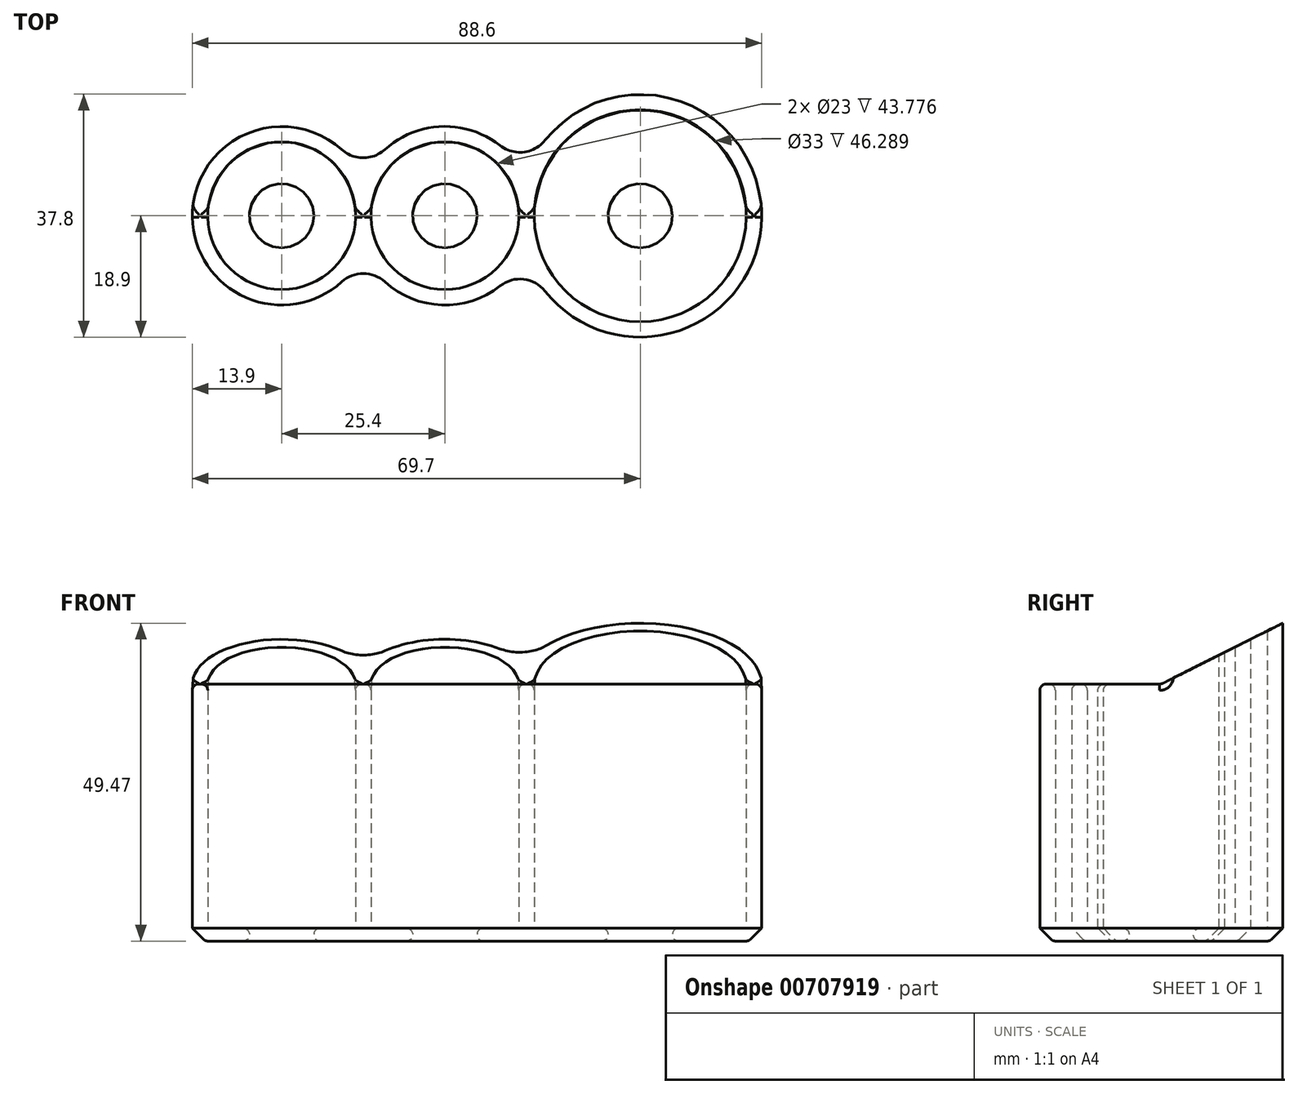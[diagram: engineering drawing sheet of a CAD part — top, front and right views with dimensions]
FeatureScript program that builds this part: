
annotation { "Feature Type Name" : "Feature", "Feature Type Description" : "" }
export const myFeature = defineFeature(function(context is Context, id is Id, definition is map)
    precondition{}
    {
        {
            var Q0;
            Q0=qCreatedBy(makeId("Top.planeOp"),FACE);
            var sketch = newSketch(context, id + "F0", { "sketchPlane" : qUnion([Q0])});
            skCircle(sketch, "E0", {"center": v(30.4, 0) * mm, "radius": 16.5 * mm});
            skCircle(sketch, "E1", {"center": v(0, 0) * mm, "radius": 11.5 * mm});
            skCircle(sketch, "E2", {"center": v(-25.4, 0) * mm, "radius": 11.5 * mm});
            skArc(sketch, "E3.0", {"start": v(-12.7, 5.65) * mm, "mid": v(-39.3, 0) * mm, "end": v(-12.7, -5.65) * mm});
            skArc(sketch, "E4.0", {"start": v(-12.7, -5.65) * mm, "mid": v(-0.23, -13.9) * mm, "end": v(12.5, -6.07) * mm});
            skArc(sketch, "E5.0", {"start": v(12.5, -6.07) * mm, "mid": v(49.3, 0) * mm, "end": v(12.5, 6.07) * mm});
            skArc(sketch, "E6.trimOffspring", {"start": v(12.5, 6.07) * mm, "mid": v(-0.23, 13.9) * mm, "end": v(-12.7, 5.65) * mm});
            skSolve(sketch);
        }
        {
            var Q0;
            Q0=qSketchRegion(id+"F0",true);
            extrude(context, id + "F1", {"entities" : qUnion([Q0]), "depth" : 50 * mm, "offsetDistance" : 25 * mm});
        }
        {
            var Q0;
            Q0=makeQuery(id+"F1.opExtrude","SWEPT_EDGE",EDGE,{"disambiguationData":[OSD([sQuery(id+"F0.wireOp",EDGE,"E3.0"),sQuery(id+"F0.wireOp",EDGE,"E4.0")])]});
            var Q1;
            Q1=makeQuery(id+"F1.opExtrude","SWEPT_EDGE",EDGE,{"disambiguationData":[OSD([sQuery(id+"F0.wireOp",EDGE,"E3.0"),sQuery(id+"F0.wireOp",EDGE,"E6.trimOffspring")])]});
            var Q2;
            Q2=makeQuery(id+"F1.opExtrude","SWEPT_EDGE",EDGE,{"disambiguationData":[OSD([sQuery(id+"F0.wireOp",EDGE,"E5.0"),sQuery(id+"F0.wireOp",EDGE,"E6.trimOffspring")])]});
            var Q3;
            Q3=makeQuery(id+"F1.opExtrude","SWEPT_EDGE",EDGE,{"disambiguationData":[OSD([sQuery(id+"F0.wireOp",EDGE,"E4.0"),sQuery(id+"F0.wireOp",EDGE,"E5.0")])]});
            fillet(context, id + "F2", {"entities" : qUnion([Q0, Q1, Q2, Q3]), "tangentPropagation" : true, "radius" : 5 * mm, "defaultsChanged" : false, "vertexSettings" : [], "allowEdgeOverflow" : false});
        }
        {
            var Q0;
            Q0=makeQuery(id+"F1.opExtrude","CAP_FACE",FACE,{"disambiguationData":[OSD([sQuery(id+"F0.wireOp",EDGE,"E0"),sQuery(id+"F0.wireOp",EDGE,"bsvTM2Ju-xRZ2-JFpn-cVXU-KiCRrkx4IUK1"),sQuery(id+"F0.wireOp",EDGE,"E1"),sQuery(id+"F0.wireOp",EDGE,"H1CsF2ZF-1dV5-S10X-kmG2-70JKXfVExCmK"),sQuery(id+"F0.wireOp",EDGE,"zndfJJh6-VviL-ZSxk-hczQ-EYFnHKfXtcnA"),sQuery(id+"F0.wireOp",EDGE,"HC5cK6VC-82Qt-4upF-mIoj-Tu8vghqNYBpw"),sQuery(id+"F0.wireOp",EDGE,"rIxCz0YV-udHC-Ne6c-NjN8-CFdPHwDd2JFN"),sQuery(id+"F0.wireOp",EDGE,"U2L2fL6y-dszB-5rkY-noFO-yn2avRcztpQ9"),sQuery(id+"F0.wireOp",EDGE,"qxlrs1d4-wGFa-lEeD-9ZLo-S0vqTRGAxUW6")])],"isStart":true});
            var sketch = newSketch(context, id + "F3", { "sketchPlane" : qUnion([Q0])});
            skCircle(sketch, "E7.0", {"center": v(-25.4, 0) * mm, "radius": 11.5 * mm});
            skCircle(sketch, "E8.0", {"center": v(0, 0) * mm, "radius": 11.5 * mm});
            skCircle(sketch, "E9", {"center": v(-25.4, 0) * mm, "radius": 5 * mm});
            skCircle(sketch, "E10", {"center": v(0, 0) * mm, "radius": 5 * mm});
            skCircle(sketch, "E11.0", {"center": v(30.4, 0) * mm, "radius": 16.5 * mm});
            skCircle(sketch, "E12", {"center": v(30.4, 0) * mm, "radius": 5 * mm});
            skSolve(sketch);
        }
        {
            var Q0;
            Q0 = qSketchRegion(id + "F3", true);
            extrude(context, id + "F4", {"entities" : qUnion([Q0]), "operationType" : NewBodyOperationType.ADD, "oppositeDirection" : true, "depth" : 2 * mm, "offsetDistance" : 25 * mm});
        }
        {
            var Q0;
            Q0=makeQuery(id+"F1.opExtrude","CAP_EDGE",EDGE,{"disambiguationData":[OSD([sQuery(id+"F0.wireOp",EDGE,"E5.0")])],"isStart":true});
            chamfer(context, id + "F5", {"entities" : qUnion([Q0]), "width" : 2 * mm, "tangentPropagation" : true});
        }
        {
            var Q0;
            Q0=qCreatedBy(makeId("Right.planeOp"),FACE);
            var sketch = newSketch(context, id + "F6", { "sketchPlane" : qUnion([Q0])});
            skLineSegment(sketch, "E13", {"start": v(19.97, 50) * mm, "end": v(0, 40) * mm});
            skLineSegment(sketch, "E14", {"start": v(-28.18, 50) * mm, "end": v(19.97, 50) * mm});
            skLineSegment(sketch, "E15.0", {"start": v(-13.9, 50) * mm, "end": v(13.9, 50) * mm, "construction": true});
            skLineSegment(sketch, "E16.0", {"start": v(-11.5, 2) * mm, "end": v(11.5, 2) * mm, "construction": true});
            skLineSegment(sketch, "E17", {"start": v(0, 40) * mm, "end": v(-28.18, 40) * mm});
            skLineSegment(sketch, "E18", {"start": v(-28.18, 40) * mm, "end": v(-28.18, 50) * mm});
            skSolve(sketch);
        }
        {
            var Q0;
            Q0 = qSketchRegion(id + "F6", true);
            extrude(context, id + "F7", {"entities" : qUnion([Q0]), "operationType" : NewBodyOperationType.REMOVE, "endBound" : BoundingType.SYMMETRIC, "oppositeDirection" : true, "depth" : 100 * mm, "offsetDistance" : 25 * mm});
        }
        {
            var Q0;
            Q0=makeQuery(id+"F7.boolean.opBoolean","COPY",FACE,{"derivedFrom":makeQuery(id+"F7.opExtrude","SWEPT_FACE",FACE,{"disambiguationData":[OSD([sQuery(id+"F6.wireOp",EDGE,"E17")])]})});
            var Q1;
            Q1=makeQuery(id+"F4.boolean.opBoolean","MERGE",FACE,{"derivedFrom":[makeQuery(id+"F1.opExtrude","CAP_FACE",FACE,{"disambiguationData":[OSD([sQuery(id+"F0.wireOp",EDGE,"E0"),sQuery(id+"F0.wireOp",EDGE,"E1"),sQuery(id+"F0.wireOp",EDGE,"E2"),sQuery(id+"F0.wireOp",EDGE,"E3.0"),sQuery(id+"F0.wireOp",EDGE,"E4.0"),sQuery(id+"F0.wireOp",EDGE,"E5.0"),sQuery(id+"F0.wireOp",EDGE,"E6.trimOffspring")])],"isStart":true}),makeQuery(id+"F4.opExtrude","CAP_FACE",FACE,{"disambiguationData":[OSD([sQuery(id+"F3.wireOp",EDGE,"E7.0"),sQuery(id+"F3.wireOp",EDGE,"E9")])],"isStart":true}),makeQuery(id+"F4.opExtrude","CAP_FACE",FACE,{"disambiguationData":[OSD([sQuery(id+"F3.wireOp",EDGE,"E8.0"),sQuery(id+"F3.wireOp",EDGE,"E10")])],"isStart":true}),makeQuery(id+"F4.opExtrude","CAP_FACE",FACE,{"disambiguationData":[OSD([sQuery(id+"F3.wireOp",EDGE,"E11.0"),sQuery(id+"F3.wireOp",EDGE,"E12")])],"isStart":true})]});
            var Q2;
            Q2=makeQuery(id+"F4.opExtrude","CAP_EDGE",EDGE,{"disambiguationData":[OSD([sQuery(id+"F3.wireOp",EDGE,"E12")])],"isStart":false});
            var Q3;
            Q3=makeQuery(id+"F4.opExtrude","CAP_EDGE",EDGE,{"disambiguationData":[OSD([sQuery(id+"F3.wireOp",EDGE,"E10")])],"isStart":false});
            var Q4;
            Q4=makeQuery(id+"F4.opExtrude","CAP_EDGE",EDGE,{"disambiguationData":[OSD([sQuery(id+"F3.wireOp",EDGE,"E9")])],"isStart":false});
            fillet(context, id + "F8", {"entities" : qUnion([Q0, Q1, Q2, Q3, Q4]), "tangentPropagation" : true, "radius" : 1 * mm, "defaultsChanged" : false, "vertexSettings" : [], "allowEdgeOverflow" : false});
        }
    });
